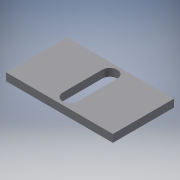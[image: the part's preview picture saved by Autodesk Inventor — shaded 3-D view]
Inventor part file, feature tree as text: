
AUTODESK INVENTOR PART (.ipt)
format: ipt  version: 2018 (Build 220112000, 112)  size: 97,280 bytes
history: native  units: mm
features: extrude x1, sketch x1
ambient origin geometry x8: Origin, YZ Plane, XZ Plane, XY Plane, X Axis, Y Axis, Z Axis, Center Point
bodies: Solid1 (feature_tree)
feature tree (2):
  extrude  "Extrusion1"  Depth=25.0mm
  sketch  "Sketch1"  dims[d6=175.0mm d7=130.0mm d8=25.0mm d9=0.0mm]
